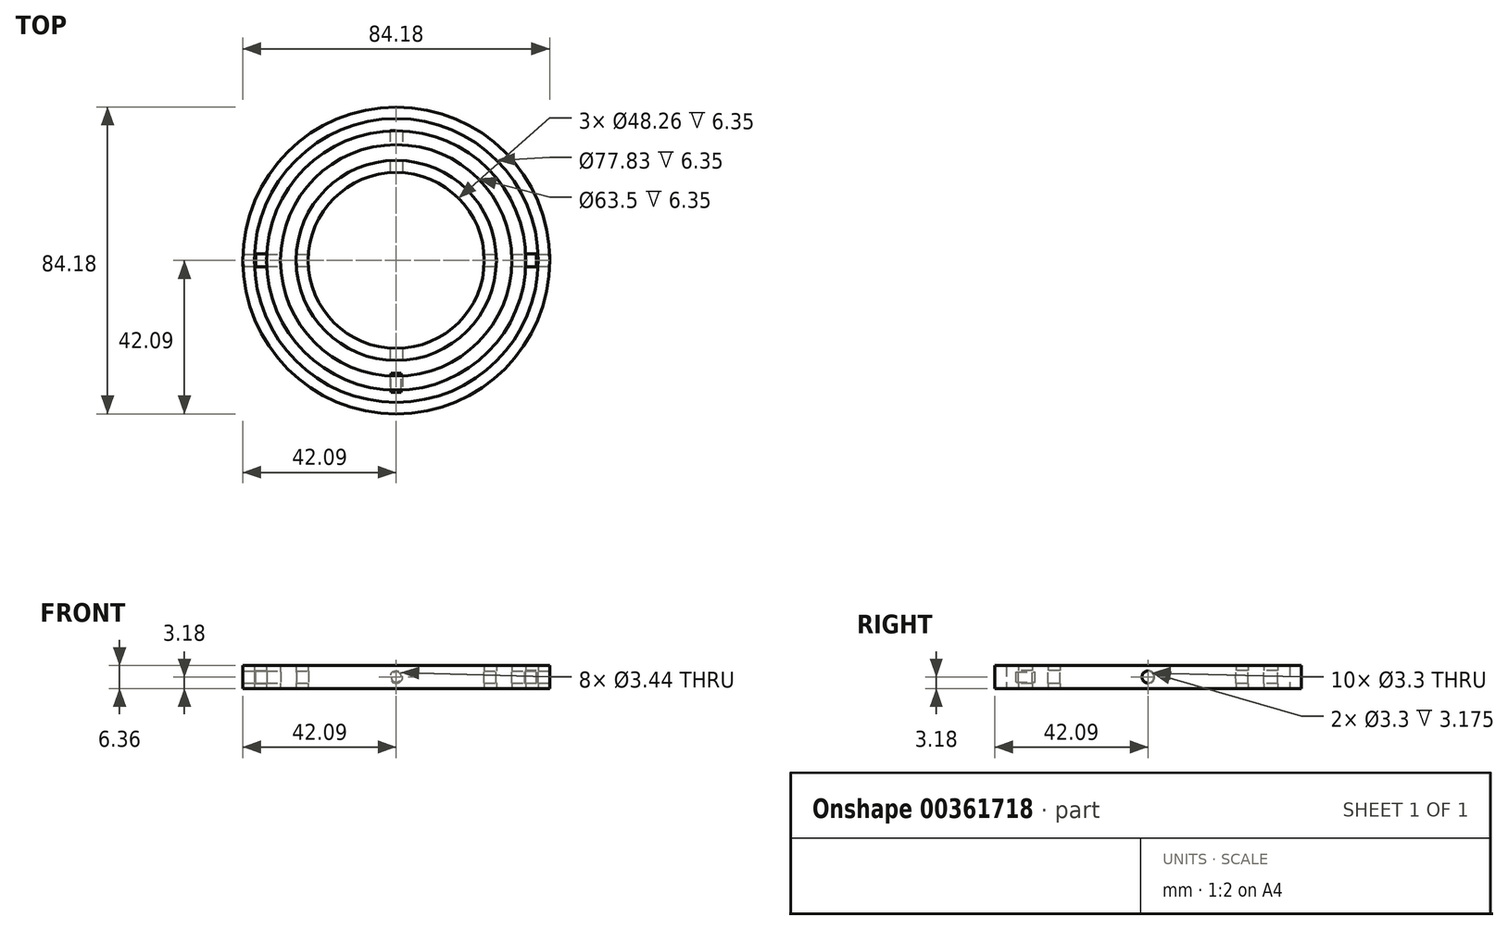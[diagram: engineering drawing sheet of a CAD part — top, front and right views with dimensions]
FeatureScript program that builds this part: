
annotation { "Feature Type Name" : "Feature", "Feature Type Description" : "" }
export const myFeature = defineFeature(function(context is Context, id is Id, definition is map)
    precondition{}
    {
        {
            var Q0;
            Q0=qCreatedBy(makeId("Top.planeOp"),FACE);
            var sketch = newSketch(context, id + "F0", { "sketchPlane" : qUnion([Q0])});
            skCircle(sketch, "E0", {"center": v(0, 0) * mm, "radius": 42.09 * mm});
            skCircle(sketch, "E1", {"center": v(0, 0) * mm, "radius": 38.91 * mm});
            skCircle(sketch, "E2", {"center": v(0, 0) * mm, "radius": 27.26 * mm});
            skCircle(sketch, "E3", {"center": v(-15.54, 44.04) * mm, "radius": 4.62 * mm});
            skCircle(sketch, "E4", {"center": v(15.24, 44.04) * mm, "radius": 4.52 * mm});
            skSolve(sketch);
        }
        {
            var Q0;
            Q0=qCreatedBy(makeId("Top.planeOp"),FACE);
            var sketch = newSketch(context, id + "F1", { "sketchPlane" : qUnion([Q0])});
            skCircle(sketch, "E5", {"center": v(0, 0) * mm, "radius": 1.59 * mm});
            skCircle(sketch, "E6", {"center": v(0, 0) * mm, "radius": 35.56 * mm});
            skCircle(sketch, "E7", {"center": v(0, 0) * mm, "radius": 31.75 * mm});
            skCircle(sketch, "E8", {"center": v(0, 0) * mm, "radius": 27.52 * mm});
            skSolve(sketch);
        }
        {
            var Q0;
            Q0=qCreatedBy(makeId("Right.planeOp"),FACE);
            cPlane(context, id + "F2", {"entities" : qUnion([Q0]), "cplaneType" : CPlaneType.OFFSET, "offset" : 42.67 * mm, "width" : 152.4 * mm, "height" : 152.4 * mm});
        }
        {
            var Q0;
            Q0=qCreatedBy(id+"F2.planeOp",FACE);
            var sketch = newSketch(context, id + "F3", { "sketchPlane" : qUnion([Q0])});
            skCircle(sketch, "E9", {"center": v(0, 0) * mm, "radius": 1.65 * mm});
            skSolve(sketch);
        }
        {
            var Q0;
            Q0=qCreatedBy(makeId("Right.planeOp"),FACE);
            cPlane(context, id + "F4", {"entities" : qUnion([Q0]), "cplaneType" : CPlaneType.OFFSET, "offset" : 35.3 * mm, "width" : 152.4 * mm, "height" : 152.4 * mm});
        }
        {
            var Q0;
            Q0=qCreatedBy(id+"F4.planeOp",FACE);
            var sketch = newSketch(context, id + "F5", { "sketchPlane" : qUnion([Q0])});
            skCircle(sketch, "E10", {"center": v(0, 0) * mm, "radius": 1.78 * mm});
            skSolve(sketch);
        }
        {
            var Q0;
            Q0=makeQuery(id+"F5.imprint","IMPRINT",FACE,{"disambiguationData":[TD([[makeQuery(id+"F5.imprint","IMPRINT",EDGE,{"derivedFrom":sQuery(id+"F5.wireOp",EDGE,"E10")}),1.0]])]});
            extrude(context, id + "F6", {"entities" : qUnion([Q0]), "depth" : 3.17 * mm});
        }
        {
            var Q0;
            Q0=makeQuery(id+"F6.opExtrude","CAP_FACE",FACE,{"disambiguationData":[OSD([sQuery(id+"F5.wireOp",EDGE,"E10")])],"isStart":false});
            var sketch = newSketch(context, id + "F7", { "sketchPlane" : qUnion([Q0])});
            skCircle(sketch, "E11", {"center": v(0, 0) * mm, "radius": 1.49 * mm});
            skSolve(sketch);
        }
        {
            var Q0;
            Q0=makeQuery(id+"F7.imprint","IMPRINT",FACE,{"disambiguationData":[TD([[makeQuery(id+"F7.imprint","IMPRINT",EDGE,{"derivedFrom":sQuery(id+"F7.wireOp",EDGE,"E11")}),1.0]])]});
            extrude(context, id + "F8", {"entities" : qUnion([Q0]), "operationType" : NewBodyOperationType.ADD, "depth" : 4.06 * mm});
        }
        {
            var Q0;
            Q0=qCreatedBy(makeId("Right.planeOp"),FACE);
            cPlane(context, id + "F9", {"entities" : qUnion([Q0]), "cplaneType" : CPlaneType.OFFSET, "offset" : 35.3 * mm, "oppositeDirection" : true, "width" : 152.4 * mm, "height" : 152.4 * mm});
        }
        {
            var Q0;
            Q0=qCreatedBy(id+"F9.planeOp",FACE);
            var sketch = newSketch(context, id + "F10", { "sketchPlane" : qUnion([Q0])});
            skCircle(sketch, "E12", {"center": v(0, 0) * mm, "radius": 1.78 * mm});
            skSolve(sketch);
        }
        {
            var Q0;
            Q0=makeQuery(id+"F10.imprint","IMPRINT",FACE,{"disambiguationData":[TD([[makeQuery(id+"F10.imprint","IMPRINT",EDGE,{"derivedFrom":sQuery(id+"F10.wireOp",EDGE,"E12")}),1.0]])]});
            extrude(context, id + "F11", {"entities" : qUnion([Q0]), "oppositeDirection" : true, "depth" : 3.17 * mm});
        }
        {
            var Q0;
            Q0=makeQuery(id+"F11.opExtrude","CAP_FACE",FACE,{"disambiguationData":[OSD([sQuery(id+"F10.wireOp",EDGE,"E12")])],"isStart":false});
            var sketch = newSketch(context, id + "F12", { "sketchPlane" : qUnion([Q0])});
            skCircle(sketch, "E13", {"center": v(0, 0) * mm, "radius": 1.49 * mm});
            skSolve(sketch);
        }
        {
            var Q0;
            Q0=makeQuery(id+"F12.imprint","IMPRINT",FACE,{"disambiguationData":[TD([[makeQuery(id+"F12.imprint","IMPRINT",EDGE,{"derivedFrom":sQuery(id+"F12.wireOp",EDGE,"E13")}),1.0]])]});
            extrude(context, id + "F13", {"entities" : qUnion([Q0]), "operationType" : NewBodyOperationType.ADD, "depth" : 4.06 * mm});
        }
        {
            var Q0;
            Q0=qCreatedBy(makeId("Top.planeOp"),FACE);
            var sketch = newSketch(context, id + "F14", { "sketchPlane" : qUnion([Q0])});
            skCircle(sketch, "E14", {"center": v(0, 0) * mm, "radius": 27.44 * mm});
            skCircle(sketch, "E15", {"center": v(0, 0) * mm, "radius": 24.13 * mm});
            skSolve(sketch);
        }
        {
            var Q0;
            Q0=makeQuery(id+"F14.imprint","IMPRINT",FACE,{"disambiguationData":[TD([[makeQuery(id+"F14.imprint","IMPRINT",EDGE,{"derivedFrom":sQuery(id+"F14.wireOp",EDGE,"E14")}),1.0]])]});
            extrude(context, id + "F15", {"entities" : qUnion([Q0]), "endBound" : BoundingType.SYMMETRIC, "depth" : 6.35 * mm});
        }
        {
            var Q0;
            Q0=qCreatedBy(makeId("Front.planeOp"),FACE);
            var sketch = newSketch(context, id + "F16", { "sketchPlane" : qUnion([Q0])});
            skCircle(sketch, "E16", {"center": v(0, 0) * mm, "radius": 1.65 * mm});
            skSolve(sketch);
        }
        {
            var Q0;
            Q0=makeQuery(id+"F16.imprint","IMPRINT",FACE,{"disambiguationData":[TD([[makeQuery(id+"F16.imprint","IMPRINT",EDGE,{"derivedFrom":sQuery(id+"F16.wireOp",EDGE,"E16")}),1.0]])]});
            extrude(context, id + "F17", {"entities" : qUnion([Q0]), "operationType" : NewBodyOperationType.REMOVE, "endBound" : BoundingType.SYMMETRIC, "oppositeDirection" : true, "depth" : 103.07 * mm});
        }
        {
            var Q0;
            Q0=qCreatedBy(makeId("Front.planeOp"),FACE);
            cPlane(context, id + "F18", {"entities" : qUnion([Q0]), "cplaneType" : CPlaneType.OFFSET, "offset" : 27.2 * mm, "width" : 152.4 * mm, "height" : 152.4 * mm});
        }
        {
            var Q0;
            Q0=qCreatedBy(id+"F18.planeOp",FACE);
            var sketch = newSketch(context, id + "F19", { "sketchPlane" : qUnion([Q0])});
            skCircle(sketch, "E17", {"center": v(0, 0) * mm, "radius": 1.65 * mm});
            skSolve(sketch);
        }
        {
            var Q0;
            Q0 = qSketchRegion(id + "F19", true);
            extrude(context, id + "F20", {"entities" : qUnion([Q0]), "operationType" : NewBodyOperationType.ADD, "depth" : 3.8 * mm});
        }
        {
            var Q0;
            Q0=makeQuery(id+"F15.opExtrude","SWEPT_BODY",BODY,{"disambiguationData":[OSD([sQuery(id+"F14.wireOp",EDGE,"E14"),sQuery(id+"F14.wireOp",EDGE,"E15")])]});
            var Q1;
            Q1=makeQuery(id+"F15.opExtrude","CAP_EDGE",EDGE,{"disambiguationData":[OSD([sQuery(id+"F14.wireOp",EDGE,"E15")])],"isStart":false});
            circularPattern(context, id + "F21", {"entities" : qUnion([Q0]), "axis" : qUnion([Q1]), "angle" : 360 * degree, "instanceCount" : 2, "equalSpace" : true});
        }
        {
            var Q0;
            Q0=makeQuery(id+"F20.opExtrude","CAP_FACE",FACE,{"disambiguationData":[OSD([sQuery(id+"F19.wireOp",EDGE,"E17")])],"isStart":false});
            var sketch = newSketch(context, id + "F22", { "sketchPlane" : qUnion([Q0])});
            skCircle(sketch, "E18", {"center": v(0, 0) * mm, "radius": 1.59 * mm});
            skSolve(sketch);
        }
        {
            var Q0;
            Q0=makeQuery(id+"F1.imprint","IMPRINT",FACE,{"disambiguationData":[TD([[makeQuery(id+"F1.imprint","IMPRINT",EDGE,{"derivedFrom":sQuery(id+"F1.wireOp",EDGE,"E6")}),1.0]])]});
            extrude(context, id + "F23", {"entities" : qUnion([Q0]), "endBound" : BoundingType.SYMMETRIC, "depth" : 6.35 * mm});
        }
        {
            var Q0;
            Q0=qCreatedBy(makeId("Front.planeOp"),FACE);
            cPlane(context, id + "F24", {"entities" : qUnion([Q0]), "cplaneType" : CPlaneType.OFFSET, "offset" : 35.64 * mm, "width" : 152.4 * mm, "height" : 152.4 * mm});
        }
        {
            var Q0;
            Q0=qCreatedBy(id+"F24.planeOp",FACE);
            var sketch = newSketch(context, id + "F25", { "sketchPlane" : qUnion([Q0])});
            skCircle(sketch, "E19", {"center": v(0, 0) * mm, "radius": 1.72 * mm});
            skSolve(sketch);
        }
        {
            var Q0;
            Q0 = qSketchRegion(id + "F25", true);
            extrude(context, id + "F26", {"entities" : qUnion([Q0]), "operationType" : NewBodyOperationType.REMOVE, "endBound" : BoundingType.THROUGH_ALL, "oppositeDirection" : true, "depth" : 3.94 * mm});
        }
        {
            var Q0;
            Q0=makeQuery(id+"F22.imprint","IMPRINT",FACE,{"disambiguationData":[TD([[makeQuery(id+"F22.imprint","IMPRINT",EDGE,{"derivedFrom":sQuery(id+"F22.wireOp",EDGE,"E18")}),1.0]])]});
            var sketch = newSketch(context, id + "F27", { "sketchPlane" : qUnion([Q0])});
            skCircle(sketch, "E20", {"center": v(0, 0) * mm, "radius": 1.4 * mm});
            skSolve(sketch);
        }
        {
            var Q0;
            Q0 = qSketchRegion(id + "F27", true);
            extrude(context, id + "F28", {"entities" : qUnion([Q0]), "operationType" : NewBodyOperationType.ADD, "depth" : 5.13 * mm});
        }
        {
            var Q0;
            Q0=makeQuery(id+"F15.opExtrude","SWEPT_BODY",BODY,{"disambiguationData":[OSD([sQuery(id+"F14.wireOp",EDGE,"E14"),sQuery(id+"F14.wireOp",EDGE,"E15")])]});
            var Q1;
            Q1=sQuery(id+"F14.wireOp",EDGE,"E15");
            circularPattern(context, id + "F29", {"entities" : qUnion([Q0]), "axis" : qUnion([Q1]), "angle" : 360 * degree, "instanceCount" : 2, "equalSpace" : true});
        }
        {
            var Q0;
            Q0=makeQuery(id+"F0.imprint","IMPRINT",FACE,{"disambiguationData":[TD([[makeQuery(id+"F0.imprint","IMPRINT",EDGE,{"derivedFrom":sQuery(id+"F0.wireOp",EDGE,"E1")}),-1.0]])]});
            extrude(context, id + "F30", {"entities" : qUnion([Q0]), "endBound" : BoundingType.SYMMETRIC, "depth" : 6.35 * mm});
        }
        {
            var Q0;
            Q0=makeQuery(id+"F3.imprint","IMPRINT",FACE,{"disambiguationData":[TD([[makeQuery(id+"F3.imprint","IMPRINT",EDGE,{"derivedFrom":sQuery(id+"F3.wireOp",EDGE,"E9")}),1.0]])]});
            extrude(context, id + "F31", {"entities" : qUnion([Q0]), "operationType" : NewBodyOperationType.REMOVE, "endBound" : BoundingType.THROUGH_ALL, "oppositeDirection" : true, "depth" : 25.4 * mm});
        }
    });
